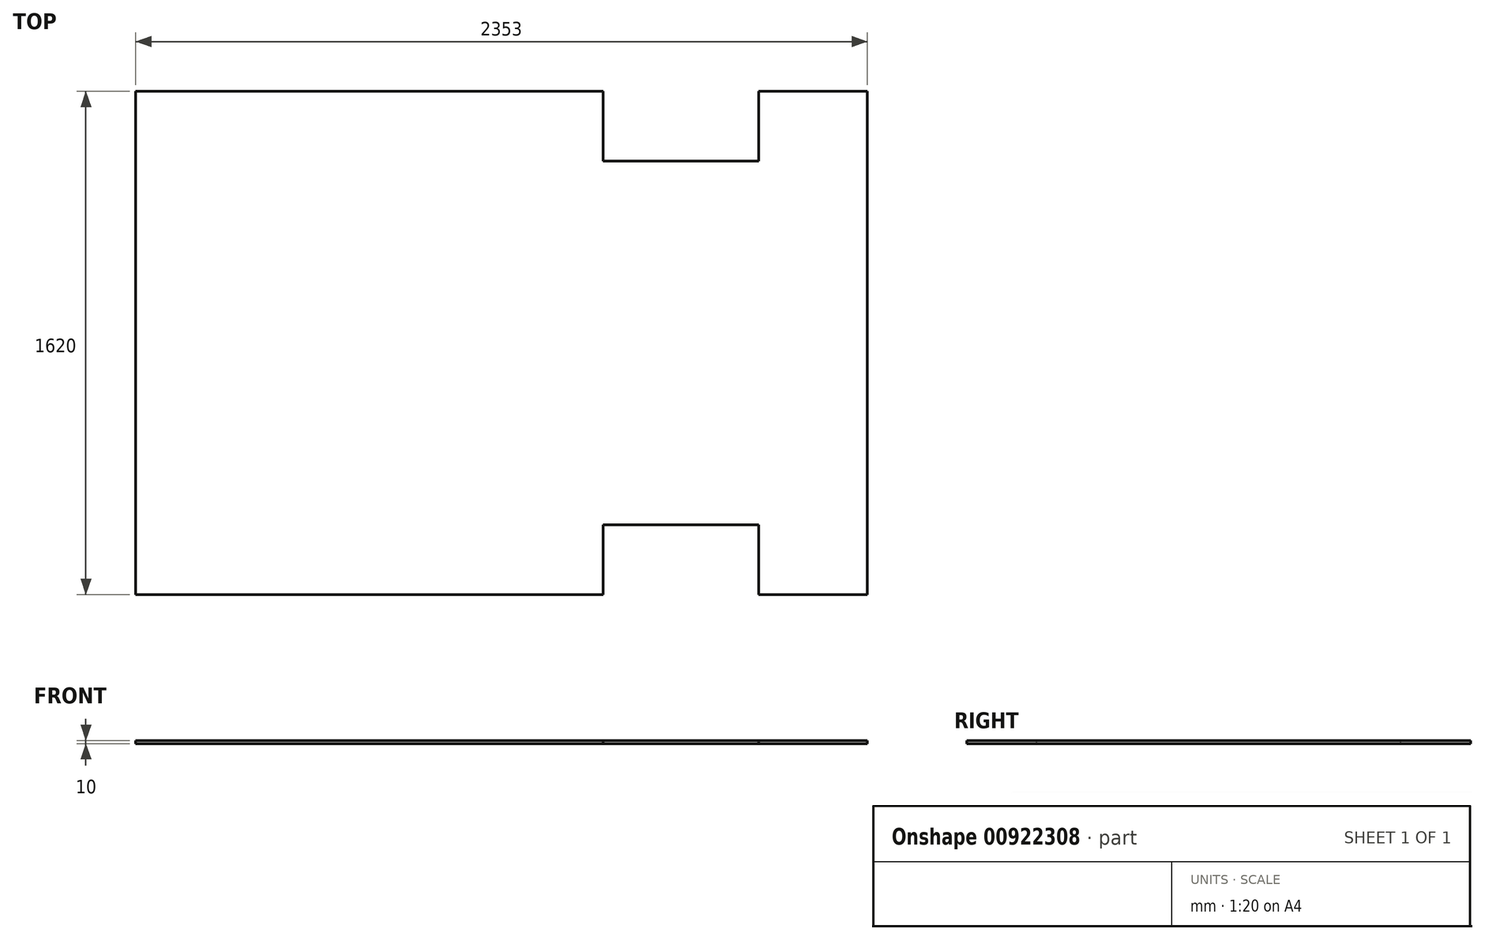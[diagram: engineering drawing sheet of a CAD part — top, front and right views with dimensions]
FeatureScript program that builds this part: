
annotation { "Feature Type Name" : "Feature", "Feature Type Description" : "" }
export const myFeature = defineFeature(function(context is Context, id is Id, definition is map)
    precondition{}
    {
        {
            var Q0;
            Q0=qCreatedBy(makeId("Top.planeOp"),FACE);
            var sketch = newSketch(context, id + "F0", { "sketchPlane" : qUnion([Q0])});
            skLineSegment(sketch, "E0", {"start": v(-2353, 0) * mm, "end": v(-2353, 1620) * mm});
            skLineSegment(sketch, "E1", {"start": v(0, 1620) * mm, "end": v(0, 0) * mm});
            skLineSegment(sketch, "E2", {"start": v(0, 0) * mm, "end": v(-350, 0) * mm});
            skLineSegment(sketch, "E3", {"start": v(-350, 0) * mm, "end": v(-350, 224) * mm});
            skLineSegment(sketch, "E4", {"start": v(-350, 224) * mm, "end": v(-850, 224) * mm});
            skLineSegment(sketch, "E5", {"start": v(-850, 0) * mm, "end": v(-2353, 0) * mm});
            skLineSegment(sketch, "E6", {"start": v(-850, 224) * mm, "end": v(-850, 0) * mm});
            skLineSegment(sketch, "E7.MirrorCS", {"start": v(-850, 1620) * mm, "end": v(-2353, 1620) * mm});
            skLineSegment(sketch, "E8.MirrorCS", {"start": v(-850, 1396) * mm, "end": v(-850, 1620) * mm});
            skLineSegment(sketch, "E9.MirrorCS", {"start": v(-350, 1396) * mm, "end": v(-850, 1396) * mm});
            skLineSegment(sketch, "E10.MirrorCS", {"start": v(-350, 1620) * mm, "end": v(-350, 1396) * mm});
            skLineSegment(sketch, "E11.MirrorCS", {"start": v(0, 1620) * mm, "end": v(-350, 1620) * mm});
            skSolve(sketch);
        }
        {
            var Q0;
            Q0=makeQuery(id+"F0.imprint","IMPRINT",FACE,{"disambiguationData":[TD([[makeQuery(id+"F0.imprint","IMPRINT",EDGE,{"derivedFrom":sQuery(id+"F0.wireOp",EDGE,"E0")}),-1.0]])]});
            var sketch = newSketch(context, id + "F1", { "sketchPlane" : qUnion([Q0])});
            skSolve(sketch);
        }
        {
            var Q0;
            Q0=makeQuery(id+"F1.imprint","IMPRINT",FACE,{"disambiguationData":[TD([[makeQuery(id+"F1.imprint","IMPRINT",EDGE,{"derivedFrom":makeQuery(id+"F0.imprint","IMPRINT",EDGE,{"derivedFrom":sQuery(id+"F0.wireOp",EDGE,"E0")})}),-1.0]])]});
            extrude(context, id + "F2", {"entities" : qUnion([Q0]), "oppositeDirection" : true, "depth" : 10 * mm, "offsetDistance" : 25 * mm});
        }
    });
